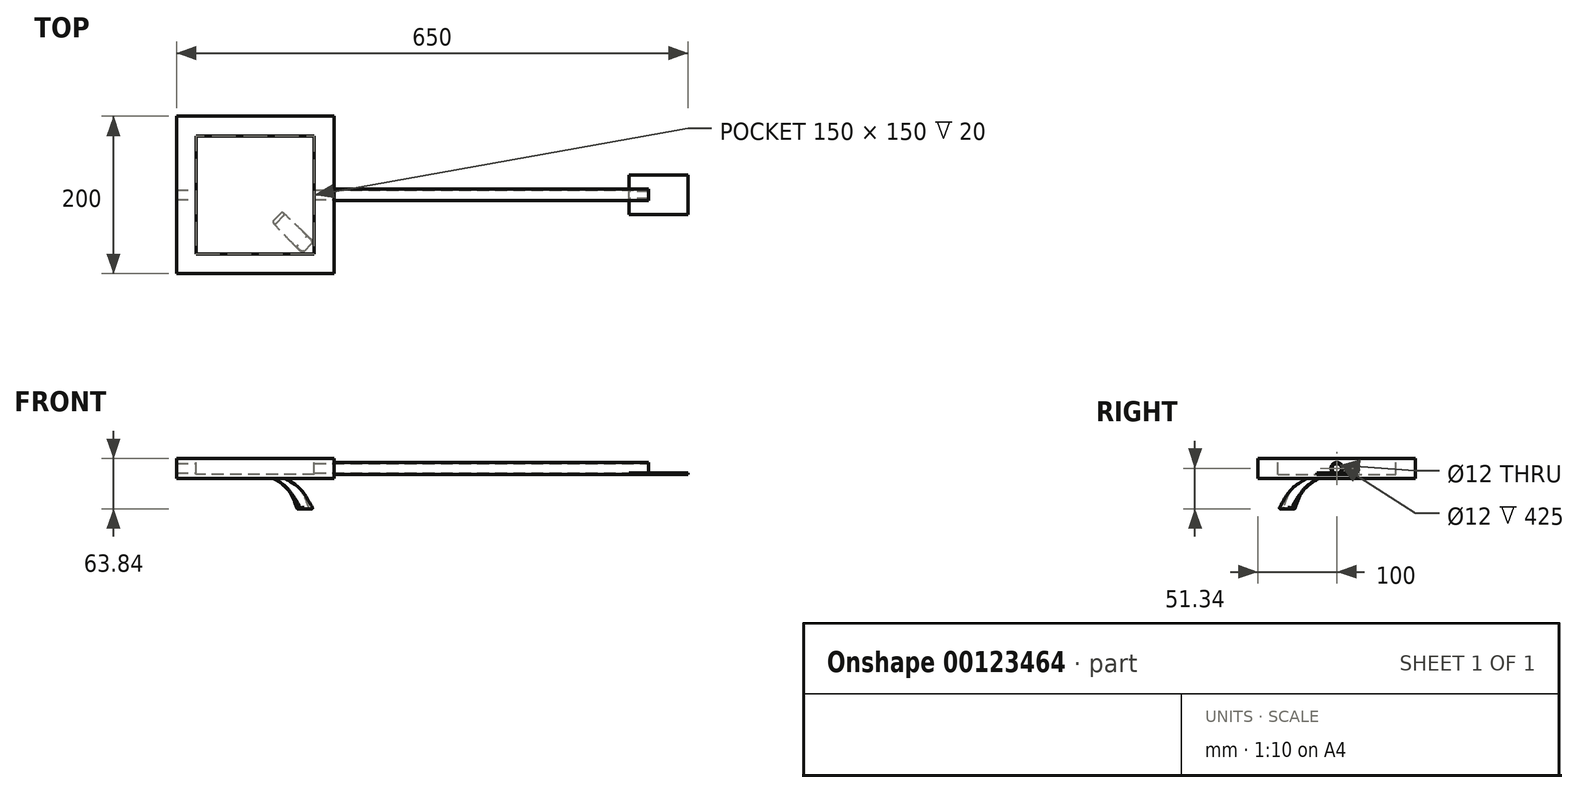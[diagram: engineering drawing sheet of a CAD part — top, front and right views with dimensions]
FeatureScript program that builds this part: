
annotation { "Feature Type Name" : "Feature", "Feature Type Description" : "" }
export const myFeature = defineFeature(function(context is Context, id is Id, definition is map)
    precondition{}
    {
        {
            var Q0;
            Q0=qCreatedBy(makeId("Top.planeOp"),FACE);
            var sketch = newSketch(context, id + "F0", { "sketchPlane" : qUnion([Q0])});
            skLineSegment(sketch, "E0.bottom", {"start": v(100, -100) * mm, "end": v(-100, -100) * mm});
            skLineSegment(sketch, "E0.top", {"start": v(100, 100) * mm, "end": v(-100, 100) * mm});
            skLineSegment(sketch, "E0.left", {"start": v(100, -100) * mm, "end": v(100, 100) * mm});
            skLineSegment(sketch, "E0.right", {"start": v(-100, -100) * mm, "end": v(-100, 100) * mm});
            skPoint(sketch, "E0.middle", {"position": v(0, 0) * mm});
            skSolve(sketch);
        }
        {
            var Q0;
            Q0 = qSketchRegion(id + "F0", true);
            var Q1;
            Q1=makeQuery(id+"F0.imprint","IMPRINT",FACE,{"disambiguationData":[TD([[makeQuery(id+"F0.imprint","IMPRINT",EDGE,{"derivedFrom":sQuery(id+"F0.wireOp",EDGE,"E0.bottom")}),-1.0]])]});
            extrude(context, id + "F1", {"entities" : qUnion([Q0, Q1]), "depth" : 25 * mm});
        }
        {
            var Q0;
            Q0=qCreatedBy(makeId("Right.planeOp"),FACE);
            var sketch = newSketch(context, id + "F2", { "sketchPlane" : qUnion([Q0])});
            skCircle(sketch, "E1", {"center": v(0, 12.5) * mm, "radius": 7.5 * mm});
            skSolve(sketch);
        }
        {
            var Q0;
            Q0 = qSketchRegion(id + "F2", true);
            extrude(context, id + "F3", {"entities" : qUnion([Q0]), "operationType" : NewBodyOperationType.ADD, "depth" : 500 * mm});
        }
        {
            var Q0;
            Q0=makeQuery(id+"F3.opExtrude","CAP_FACE",FACE,{"disambiguationData":[OSD([sQuery(id+"F2.wireOp",EDGE,"E1")])],"isStart":false});
            var sketch = newSketch(context, id + "F4", { "sketchPlane" : qUnion([Q0])});
            skCircle(sketch, "E2", {"center": v(0, 12.5) * mm, "radius": 6 * mm});
            skSolve(sketch);
        }
        {
            var Q0;
            Q0 = qSketchRegion(id + "F4", true);
            extrude(context, id + "F5", {"entities" : qUnion([Q0]), "operationType" : NewBodyOperationType.REMOVE, "endBound" : BoundingType.UP_TO_NEXT, "oppositeDirection" : true, "depth" : 420 * mm});
        }
        {
            var Q0;
            Q0=makeQuery(id+"F3.opExtrude","CAP_FACE",FACE,{"disambiguationData":[OSD([sQuery(id+"F2.wireOp",EDGE,"E1")])],"isStart":false});
            var sketch = newSketch(context, id + "F6", { "sketchPlane" : qUnion([Q0])});
            skLineSegment(sketch, "E3.bottom", {"start": v(-25, 5) * mm, "end": v(25, 5) * mm});
            skLineSegment(sketch, "E3.top", {"start": v(-25, 6.5) * mm, "end": v(25, 6.5) * mm});
            skLineSegment(sketch, "E3.left", {"start": v(-25, 5) * mm, "end": v(-25, 6.5) * mm});
            skLineSegment(sketch, "E3.right", {"start": v(25, 5) * mm, "end": v(25, 6.5) * mm});
            skPoint(sketch, "E3.middle", {"position": v(0, 5.75) * mm});
            skSolve(sketch);
        }
        {
            var Q0;
            Q0 = qSketchRegion(id + "F6", true);
            extrude(context, id + "F7", {"entities" : qUnion([Q0]), "operationType" : NewBodyOperationType.ADD, "depth" : 50 * mm, "hasSecondDirection" : true, "secondDirectionOppositeDirection" : true, "secondDirectionDepth" : 25 * mm});
        }
        {
            var Q0;
            Q0=makeQuery(id+"F1.opExtrude","CAP_FACE",FACE,{"disambiguationData":[OSD([sQuery(id+"F0.wireOp",EDGE,"E0.bottom"),sQuery(id+"F0.wireOp",EDGE,"E0.top"),sQuery(id+"F0.wireOp",EDGE,"E0.left"),sQuery(id+"F0.wireOp",EDGE,"E0.right")])],"isStart":false});
            var sketch = newSketch(context, id + "F8", { "sketchPlane" : qUnion([Q0])});
            skCircle(sketch, "E4", {"center": v(0, 0) * mm, "radius": 21.04 * mm});
            skSolve(sketch);
        }
        {
            var Q0;
            Q0=makeQuery(id+"F1.opExtrude","CAP_FACE",FACE,{"disambiguationData":[OSD([sQuery(id+"F0.wireOp",EDGE,"E0.bottom"),sQuery(id+"F0.wireOp",EDGE,"E0.top"),sQuery(id+"F0.wireOp",EDGE,"E0.left"),sQuery(id+"F0.wireOp",EDGE,"E0.right")])],"isStart":false});
            var sketch = newSketch(context, id + "F9", { "sketchPlane" : qUnion([Q0])});
            skLineSegment(sketch, "E5.bottom", {"start": v(75, -75) * mm, "end": v(-75, -75) * mm});
            skLineSegment(sketch, "E5.top", {"start": v(75, 75) * mm, "end": v(-75, 75) * mm});
            skLineSegment(sketch, "E5.left", {"start": v(75, -75) * mm, "end": v(75, 75) * mm});
            skLineSegment(sketch, "E5.right", {"start": v(-75, -75) * mm, "end": v(-75, 75) * mm});
            skPoint(sketch, "E5.middle", {"position": v(0, 0) * mm});
            skSolve(sketch);
        }
        {
            var Q0;
            Q0 = qSketchRegion(id + "F9", true);
            extrude(context, id + "F10", {"entities" : qUnion([Q0]), "operationType" : NewBodyOperationType.REMOVE, "oppositeDirection" : true, "depth" : 20 * mm});
        }
        {
            var Q0;
            Q0=makeQuery(id+"F10.boolean.opBoolean","COPY",VERTEX,{"derivedFrom":makeQuery(id+"F10.opExtrude","CAP_VERTEX",VERTEX,{"disambiguationData":[OSD([sQuery(id+"F9.wireOp",EDGE,"E5.top"),sQuery(id+"F9.wireOp",EDGE,"E5.right")])],"isStart":true})});
            var Q1;
            Q1=makeQuery(id+"F10.boolean.opBoolean","COPY",VERTEX,{"derivedFrom":makeQuery(id+"F10.opExtrude","CAP_VERTEX",VERTEX,{"disambiguationData":[OSD([sQuery(id+"F9.wireOp",EDGE,"E5.bottom"),sQuery(id+"F9.wireOp",EDGE,"E5.left")])],"isStart":true})});
            var Q2;
            Q2=qCreatedBy(makeId("Origin.pointOp"),VERTEX);
            cPlane(context, id + "F11", {"entities" : qUnion([Q0, Q1, Q2]), "cplaneType" : CPlaneType.THREE_POINT, "offset" : 25 * mm, "width" : 150 * mm, "height" : 150 * mm});
        }
        {
            var Q0;
            Q0=qCreatedBy(id+"F11.planeOp",FACE);
            var sketch = newSketch(context, id + "F12", { "sketchPlane" : qUnion([Q0])});
            skFitSpline(sketch, "E6", {"points": [v(44.55, 0) * mm, v(73.5, -13.96) * mm, v(95.79, -38.84) * mm], "startDerivative": vector(62.02, -22.97) * mm, "endDerivative": vector(40.51, -54.6) * mm});
            skLineSegment(sketch, "E7", {"start": v(95.79, -38.84) * mm, "end": v(83.53, -38.84) * mm});
            skFitSpline(sketch, "E8", {"points": [v(83.53, -38.84) * mm, v(69.05, -16.56) * mm, v(39.72, 0) * mm], "startDerivative": vector(-25, 51.14) * mm, "endDerivative": vector(-61.9, 27) * mm});
            skLineSegment(sketch, "E9", {"start": v(44.55, 0) * mm, "end": v(39.72, 0) * mm});
            skSolve(sketch);
        }
        {
            var Q0;
            Q0 = qSketchRegion(id + "F12", true);
            extrude(context, id + "F13", {"entities" : qUnion([Q0]), "operationType" : NewBodyOperationType.ADD, "depth" : 10 * mm, "hasSecondDirection" : true, "secondDirectionOppositeDirection" : true, "secondDirectionDepth" : 10 * mm});
        }
        {
            var Q0;
            Q0=makeQuery(id+"F13.opExtrude","CAP_EDGE",EDGE,{"disambiguationData":[OSD([sQuery(id+"F12.wireOp",EDGE,"E6")])],"isStart":false});
            var Q1;
            Q1=makeQuery(id+"F13.opExtrude","CAP_EDGE",EDGE,{"disambiguationData":[OSD([sQuery(id+"F12.wireOp",EDGE,"E8")])],"isStart":false});
            var Q2;
            Q2=makeQuery(id+"F13.opExtrude","CAP_EDGE",EDGE,{"disambiguationData":[OSD([sQuery(id+"F12.wireOp",EDGE,"E6")])],"isStart":true});
            var Q3;
            Q3=makeQuery(id+"F13.opExtrude","CAP_EDGE",EDGE,{"disambiguationData":[OSD([sQuery(id+"F12.wireOp",EDGE,"E8")])],"isStart":true});
            fillet(context, id + "F14", {"entities" : qUnion([Q0, Q1, Q2, Q3]), "radius" : 3 * mm, "tangentPropagation" : true, "allowEdgeOverflow" : false});
        }
        {
            var Q0;
            Q0=makeQuery(id+"F10.boolean.opBoolean","COPY",FACE,{"derivedFrom":makeQuery(id+"F10.opExtrude","CAP_FACE",FACE,{"disambiguationData":[OSD([sQuery(id+"F9.wireOp",EDGE,"E5.bottom"),sQuery(id+"F9.wireOp",EDGE,"E5.top"),sQuery(id+"F9.wireOp",EDGE,"E5.left"),sQuery(id+"F9.wireOp",EDGE,"E5.right")])],"isStart":false})});
            var sketch = newSketch(context, id + "F15", { "sketchPlane" : qUnion([Q0])});
            skCircle(sketch, "E10", {"center": v(0, 0) * mm, "radius": 25.54 * mm});
            skSolve(sketch);
        }
        {
            var Q0;
            Q0=makeQuery(id+"F13.opExtrude","SWEPT_FACE",FACE,{"disambiguationData":[OSD([sQuery(id+"F12.wireOp",EDGE,"E7")])]});
            var Q1;
            Q1=makeQuery(id+"FOgQDJa9XkEuTwu_1.3.F13.opExtrude","SWEPT_FACE",FACE,{"disambiguationData":[OSD([sQuery(id+"F12.wireOp",EDGE,"E7")])]});
            var Q2;
            Q2=makeQuery(id+"FOgQDJa9XkEuTwu_1.2.F13.opExtrude","SWEPT_FACE",FACE,{"disambiguationData":[OSD([sQuery(id+"F12.wireOp",EDGE,"E7")])]});
            var Q3;
            Q3=makeQuery(id+"FOgQDJa9XkEuTwu_1.1.F13.opExtrude","SWEPT_FACE",FACE,{"disambiguationData":[OSD([sQuery(id+"F12.wireOp",EDGE,"E7")])]});
            fillet(context, id + "F16", {"entities" : qUnion([Q0, Q1, Q2, Q3]), "radius" : 1 * mm, "tangentPropagation" : true, "allowEdgeOverflow" : false});
        }
    });
